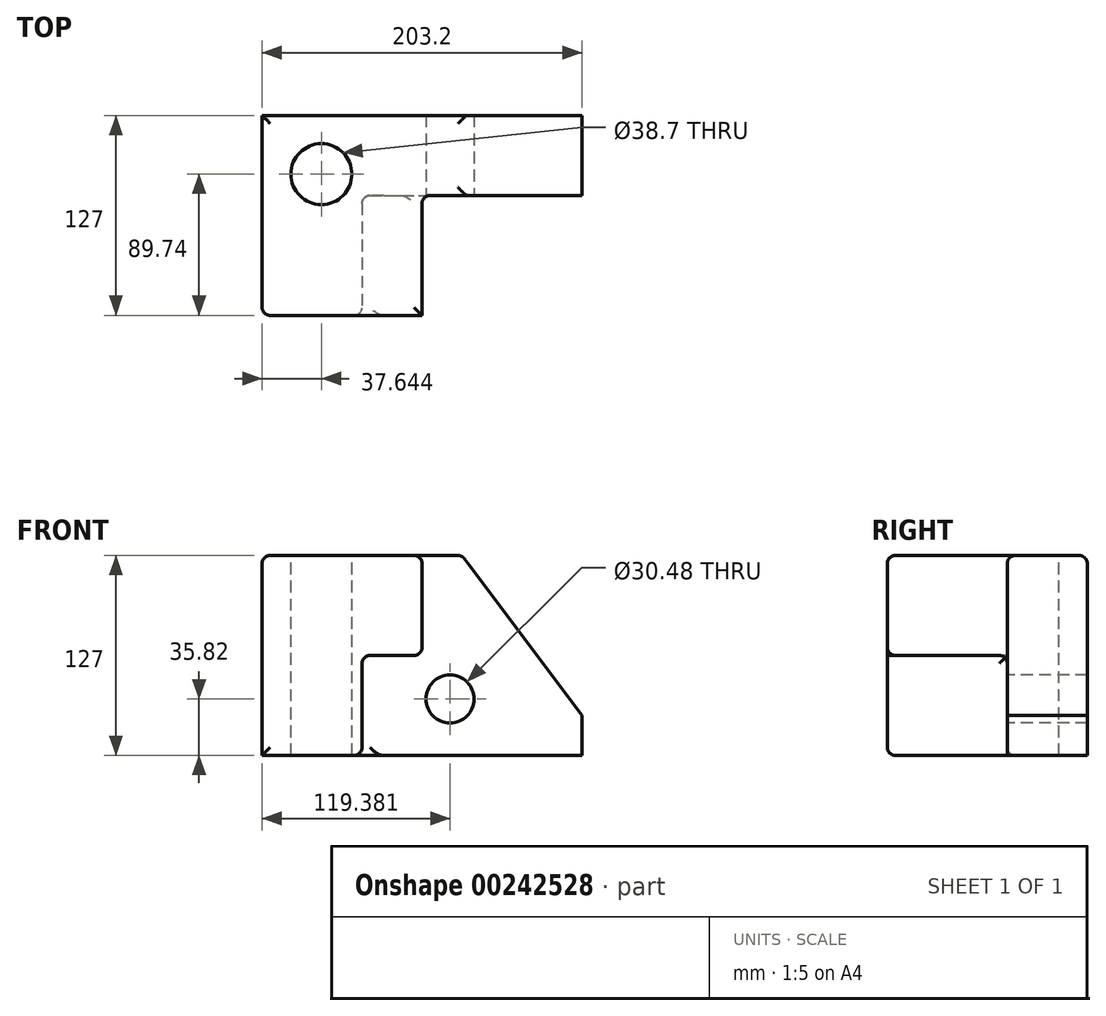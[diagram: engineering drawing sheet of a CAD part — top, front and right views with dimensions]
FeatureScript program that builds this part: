
annotation { "Feature Type Name" : "Feature", "Feature Type Description" : "" }
export const myFeature = defineFeature(function(context is Context, id is Id, definition is map)
    precondition{}
    {
        {
            var Q0;
            Q0=qCreatedBy(makeId("Front.planeOp"),FACE);
            var sketch = newSketch(context, id + "F0", { "sketchPlane" : qUnion([Q0])});
            skLineSegment(sketch, "E0.bottom", {"start": v(-62.68, 91.18) * mm, "end": v(140.52, 91.18) * mm});
            skLineSegment(sketch, "E0.top", {"start": v(-62.68, -35.82) * mm, "end": v(140.52, -35.82) * mm});
            skLineSegment(sketch, "E0.left", {"start": v(-62.68, 91.18) * mm, "end": v(-62.68, -35.82) * mm});
            skLineSegment(sketch, "E0.right", {"start": v(140.52, 91.18) * mm, "end": v(140.52, -35.82) * mm});
            skSolve(sketch);
        }
        {
            var Q0;
            Q0 = qSketchRegion(id + "F0", true);
            extrude(context, id + "F1", {"entities" : qUnion([Q0]), "depth" : 127 * mm});
        }
        {
            var Q0;
            Q0=makeQuery(id+"F1.opExtrude","CAP_FACE",FACE,{"disambiguationData":[OSD([sQuery(id+"F0.wireOp",EDGE,"E0.bottom"),sQuery(id+"F0.wireOp",EDGE,"E0.top"),sQuery(id+"F0.wireOp",EDGE,"E0.left"),sQuery(id+"F0.wireOp",EDGE,"E0.right")])],"isStart":false});
            var sketch = newSketch(context, id + "F2", { "sketchPlane" : qUnion([Q0])});
            skLineSegment(sketch, "E1", {"start": v(0.82, 27.68) * mm, "end": v(38.92, 27.68) * mm});
            skLineSegment(sketch, "E2", {"start": v(38.92, 27.68) * mm, "end": v(38.92, 91.18) * mm});
            skLineSegment(sketch, "E3", {"start": v(0.82, 27.68) * mm, "end": v(0.82, -35.82) * mm});
            skLineSegment(sketch, "E4", {"start": v(-62.68, 91.18) * mm, "end": v(38.92, 91.18) * mm});
            skLineSegment(sketch, "E5", {"start": v(-62.68, 91.18) * mm, "end": v(-62.68, -35.82) * mm});
            skLineSegment(sketch, "E6", {"start": v(-62.68, -35.82) * mm, "end": v(0.82, -35.82) * mm});
            skSolve(sketch);
        }
        {
            var Q0;
            Q0=makeQuery(id+"F2.imprint","IMPRINT",FACE,{"disambiguationData":[TD([[makeQuery(id+"F2.imprint","IMPRINT",EDGE,{"derivedFrom":sQuery(id+"F2.wireOp",EDGE,"E1")}),-1.0]])]});
            extrude(context, id + "F3", {"entities" : qUnion([Q0]), "operationType" : NewBodyOperationType.REMOVE, "oppositeDirection" : true, "depth" : 76.2 * mm});
        }
        {
            var Q0;
            Q0=makeQuery(id+"F1.opExtrude","SWEPT_EDGE",EDGE,{"disambiguationData":[OSD([sQuery(id+"F0.wireOp",EDGE,"E0.bottom"),sQuery(id+"F0.wireOp",EDGE,"E0.right")])]});
            chamfer(context, id + "F4", {"entities" : qUnion([Q0]), "chamferType" : ChamferType.TWO_OFFSETS, "width1" : 76.2 * mm, "oppositeDirection" : false, "width2" : 101.6 * mm, "tangentPropagation" : true});
        }
        {
            var Q0;
            Q0=makeQuery(id+"F1.opExtrude","CAP_EDGE",EDGE,{"disambiguationData":[OSD([sQuery(id+"F0.wireOp",EDGE,"E0.bottom")])],"isStart":false});
            var Q1;
            Q1=makeQuery(id+"F3.boolean.opBoolean","COPY",EDGE,{"derivedFrom":makeQuery(id+"F3.opExtrude","CAP_EDGE",EDGE,{"disambiguationData":[OSD([sQuery(id+"F2.wireOp",EDGE,"E2")])],"isStart":true})});
            var Q2;
            Q2=makeQuery(id+"F3.boolean.opBoolean","COPY",EDGE,{"derivedFrom":makeQuery(id+"F3.opExtrude","CAP_EDGE",EDGE,{"disambiguationData":[OSD([sQuery(id+"F2.wireOp",EDGE,"E1")])],"isStart":true})});
            var Q3;
            Q3=makeQuery(id+"F3.boolean.opBoolean","COPY",EDGE,{"derivedFrom":makeQuery(id+"F3.opExtrude","CAP_EDGE",EDGE,{"disambiguationData":[OSD([sQuery(id+"F2.wireOp",EDGE,"E3")])],"isStart":true})});
            var Q4;
            Q4=makeQuery(id+"F3.boolean.opBoolean","COPY",EDGE,{"derivedFrom":makeQuery(id+"F3.opExtrude","SWEPT_EDGE",EDGE,{"disambiguationData":[OSD([sQuery(id+"F2.wireOp",EDGE,"E1"),sQuery(id+"F2.wireOp",EDGE,"E2")])]})});
            var Q5;
            Q5=makeQuery(id+"F1.opExtrude","CAP_EDGE",EDGE,{"disambiguationData":[OSD([sQuery(id+"F0.wireOp",EDGE,"E0.left")])],"isStart":false});
            var Q6;
            Q6=makeQuery(id+"F3.boolean.opBoolean","COPY",FACE,{"derivedFrom":makeQuery(id+"F3.opExtrude","SWEPT_FACE",FACE,{"disambiguationData":[OSD([sQuery(id+"F2.wireOp",EDGE,"E3")])]})});
            var Q7;
            Q7=makeQuery(id+"F3.boolean.opBoolean","COPY",EDGE,{"derivedFrom":makeQuery(id+"F3.opExtrude","CAP_EDGE",EDGE,{"disambiguationData":[OSD([sQuery(id+"F2.wireOp",EDGE,"E2")])],"isStart":false})});
            var Q8;
            Q8=makeQuery(id+"F3.boolean.opBoolean","COPY",EDGE,{"derivedFrom":makeQuery(id+"F3.opExtrude","SWEPT_EDGE",EDGE,{"disambiguationData":[OSD([sQuery(id+"F0.wireOp",EDGE,"E0.bottom"),sQuery(id+"F2.wireOp",EDGE,"E2"),sQuery(id+"F2.wireOp",EDGE,"E4")])]})});
            var Q9;
            Q9=makeQuery(id+"F1.opExtrude","SWEPT_FACE",FACE,{"disambiguationData":[OSD([sQuery(id+"F0.wireOp",EDGE,"E0.bottom")])]});
            var Q10;
            Q10=makeQuery(id+"F1.opExtrude","CAP_EDGE",EDGE,{"disambiguationData":[OSD([sQuery(id+"F0.wireOp",EDGE,"E0.top")])],"isStart":false});
            var Q11;
            Q11=makeQuery(id+"F3.boolean.opBoolean","COPY",EDGE,{"derivedFrom":makeQuery(id+"F3.opExtrude","SWEPT_EDGE",EDGE,{"disambiguationData":[OSD([sQuery(id+"F0.wireOp",EDGE,"E0.top"),sQuery(id+"F2.wireOp",EDGE,"E3"),sQuery(id+"F2.wireOp",EDGE,"E6")])]})});
            fillet(context, id + "F5", {"entities" : qUnion([Q0, Q1, Q2, Q3, Q4, Q5, Q6, Q7, Q8, Q9, Q10, Q11]), "radius" : 5.08 * mm, "tangentPropagation" : true, "allowEdgeOverflow" : false});
        }
        {
            var Q0;
            Q0=makeQuery(id+"F3.boolean.opBoolean","COPY",FACE,{"derivedFrom":makeQuery(id+"F3.opExtrude","CAP_FACE",FACE,{"disambiguationData":[OSD([sQuery(id+"F0.wireOp",EDGE,"E0.bottom"),sQuery(id+"F0.wireOp",EDGE,"E0.top"),sQuery(id+"F0.wireOp",EDGE,"E0.right"),sQuery(id+"F2.wireOp",EDGE,"E1"),sQuery(id+"F2.wireOp",EDGE,"E2"),sQuery(id+"F2.wireOp",EDGE,"E3")])],"isStart":false})});
            var sketch = newSketch(context, id + "F6", { "sketchPlane" : qUnion([Q0])});
            skCircle(sketch, "E7", {"center": v(56.7, 0) * mm, "radius": 15.24 * mm});
            skSolve(sketch);
        }
        {
            var Q0;
            Q0=makeQuery(id+"F6.imprint","IMPRINT",FACE,{"disambiguationData":[TD([[makeQuery(id+"F6.imprint","IMPRINT",EDGE,{"derivedFrom":sQuery(id+"F6.wireOp",EDGE,"E7")}),1.0]])]});
            var Q1;
            Q1=makeQuery(id+"F1.opExtrude","CAP_FACE",FACE,{"disambiguationData":[OSD([sQuery(id+"F0.wireOp",EDGE,"E0.bottom"),sQuery(id+"F0.wireOp",EDGE,"E0.top"),sQuery(id+"F0.wireOp",EDGE,"E0.left"),sQuery(id+"F0.wireOp",EDGE,"E0.right")])],"isStart":true});
            extrude(context, id + "F7", {"entities" : qUnion([Q0]), "operationType" : NewBodyOperationType.REMOVE, "endBound" : BoundingType.UP_TO_SURFACE, "oppositeDirection" : true, "endBoundEntityFace" : qUnion([Q1]), "depth" : 25.4 * mm});
        }
        {
            var Q0;
            Q0=makeQuery(id+"F1.opExtrude","SWEPT_FACE",FACE,{"disambiguationData":[OSD([sQuery(id+"F0.wireOp",EDGE,"E0.bottom")])]});
            var sketch = newSketch(context, id + "F8", { "sketchPlane" : qUnion([Q0])});
            skCircle(sketch, "E8", {"center": v(-25.04, -37.26) * mm, "radius": 19.35 * mm});
            skSolve(sketch);
        }
        {
            var Q0;
            Q0=makeQuery(id+"F8.imprint","IMPRINT",FACE,{"disambiguationData":[TD([[makeQuery(id+"F8.imprint","IMPRINT",EDGE,{"derivedFrom":sQuery(id+"F8.wireOp",EDGE,"E8")}),1.0]])]});
            var Q1;
            Q1=makeQuery(id+"F1.opExtrude","SWEPT_FACE",FACE,{"disambiguationData":[OSD([sQuery(id+"F0.wireOp",EDGE,"E0.top")])]});
            extrude(context, id + "F9", {"entities" : qUnion([Q0]), "operationType" : NewBodyOperationType.REMOVE, "endBound" : BoundingType.UP_TO_SURFACE, "oppositeDirection" : true, "endBoundEntityFace" : qUnion([Q1]), "depth" : 25.4 * mm});
        }
    });
